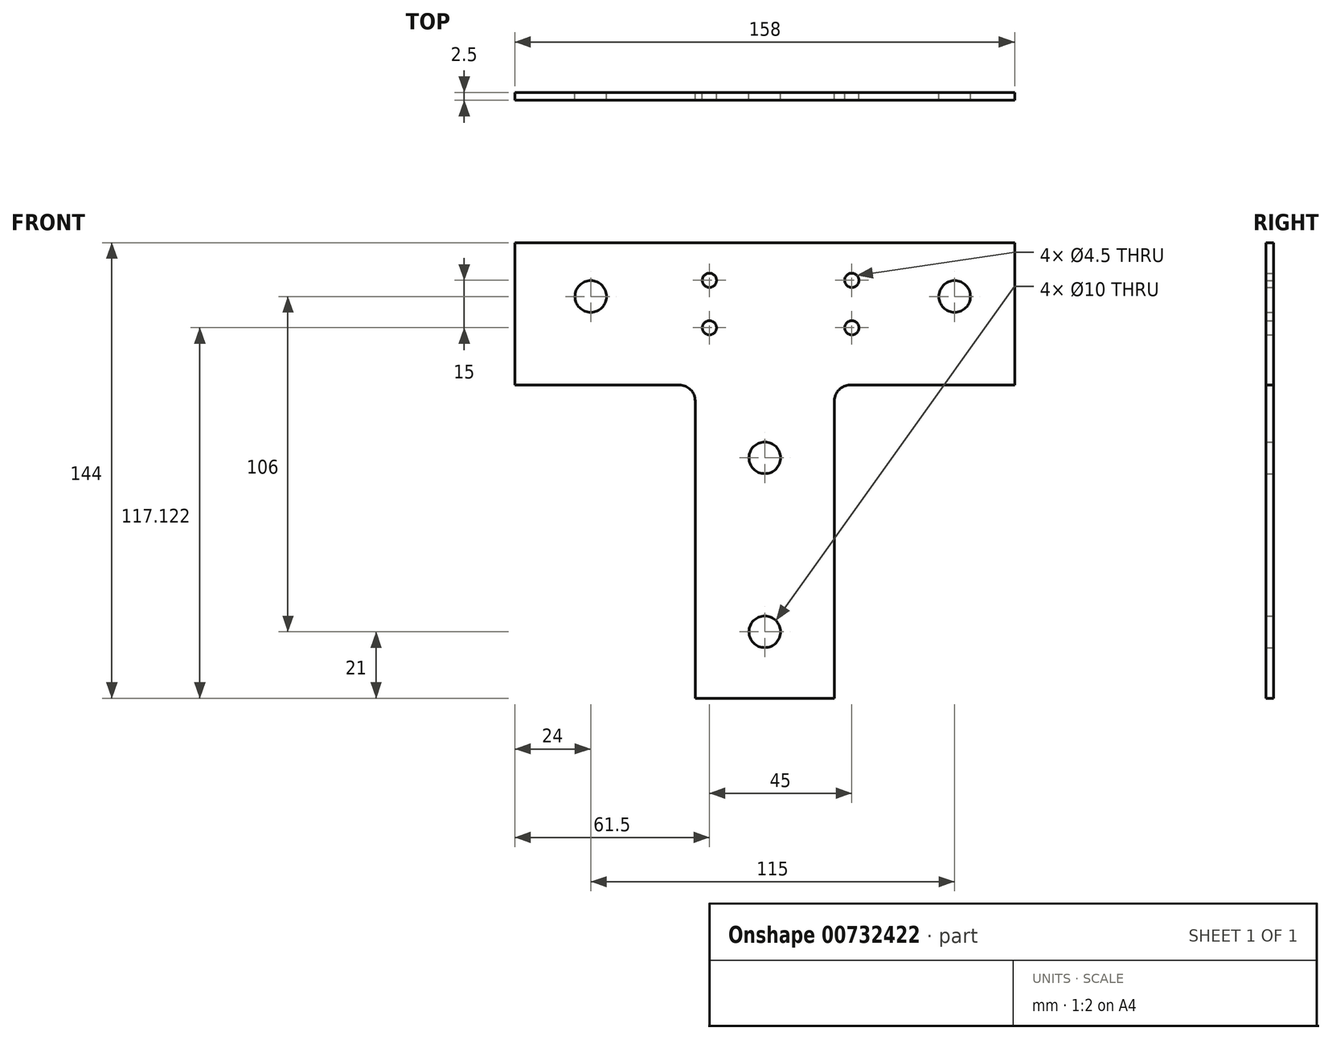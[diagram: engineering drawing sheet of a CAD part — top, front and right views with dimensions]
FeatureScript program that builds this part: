
annotation { "Feature Type Name" : "Feature", "Feature Type Description" : "" }
export const myFeature = defineFeature(function(context is Context, id is Id, definition is map)
    precondition{}
    {
        {
            var Q0;
            Q0=qCreatedBy(makeId("Front.planeOp"),FACE);
            var sketch = newSketch(context, id + "F0", { "sketchPlane" : qUnion([Q0])});
            skLineSegment(sketch, "E0.bottom", {"start": v(79, 49.5) * mm, "end": v(22, 49.5) * mm});
            skLineSegment(sketch, "E0.top", {"start": v(79, 94.5) * mm, "end": v(-79, 94.5) * mm});
            skLineSegment(sketch, "E0.left", {"start": v(79, 49.5) * mm, "end": v(79, 94.5) * mm});
            skLineSegment(sketch, "E0.right", {"start": v(-79, 49.5) * mm, "end": v(-79, 94.5) * mm});
            skPoint(sketch, "E0.middle", {"position": v(0, 72) * mm});
            skLineSegment(sketch, "E1.top", {"start": v(22, -49.5) * mm, "end": v(-22, -49.5) * mm});
            skLineSegment(sketch, "E1.left", {"start": v(22, 49.5) * mm, "end": v(22, -49.5) * mm});
            skLineSegment(sketch, "E1.right", {"start": v(-22, 49.5) * mm, "end": v(-22, -49.5) * mm});
            skPoint(sketch, "E1.middle", {"position": v(0, 0) * mm});
            skLineSegment(sketch, "E2.trimOffspring", {"start": v(-22, 49.5) * mm, "end": v(-79, 49.5) * mm});
            skCircle(sketch, "E3", {"center": v(0, -28.5) * mm, "radius": 5 * mm});
            skCircle(sketch, "E4", {"center": v(0, 26.5) * mm, "radius": 5 * mm});
            skCircle(sketch, "E5", {"center": v(60, 77.5) * mm, "radius": 5 * mm});
            skCircle(sketch, "E6", {"center": v(-55, 77.5) * mm, "radius": 5 * mm});
            skCircle(sketch, "E7", {"center": v(27.5, 82.62) * mm, "radius": 2.25 * mm});
            skCircle(sketch, "E8", {"center": v(-17.5, 82.62) * mm, "radius": 2.25 * mm});
            skCircle(sketch, "E9", {"center": v(-17.5, 67.62) * mm, "radius": 2.25 * mm});
            skCircle(sketch, "E10", {"center": v(27.5, 67.62) * mm, "radius": 2.25 * mm});
            skSolve(sketch);
        }
        {
            var Q0;
            Q0 = qSketchRegion(id + "F0", true);
            extrude(context, id + "F1", {"entities" : qUnion([Q0]), "depth" : 2.5 * mm, "offsetDistance" : 25 * mm});
        }
        {
            var Q0;
            Q0=makeQuery(id+"F1.opExtrude","SWEPT_EDGE",EDGE,{"disambiguationData":[OSD([sQuery(id+"F0.wireOp",EDGE,"E0.bottom"),sQuery(id+"F0.wireOp",EDGE,"E1.left")])]});
            var Q1;
            Q1=makeQuery(id+"F1.opExtrude","SWEPT_EDGE",EDGE,{"disambiguationData":[OSD([sQuery(id+"F0.wireOp",EDGE,"E1.right"),sQuery(id+"F0.wireOp",EDGE,"E2.trimOffspring")])]});
            fillet(context, id + "F2", {"entities" : qUnion([Q0, Q1]), "radius" : 5 * mm, "tangentPropagation" : true, "allowEdgeOverflow" : false});
        }
    });
